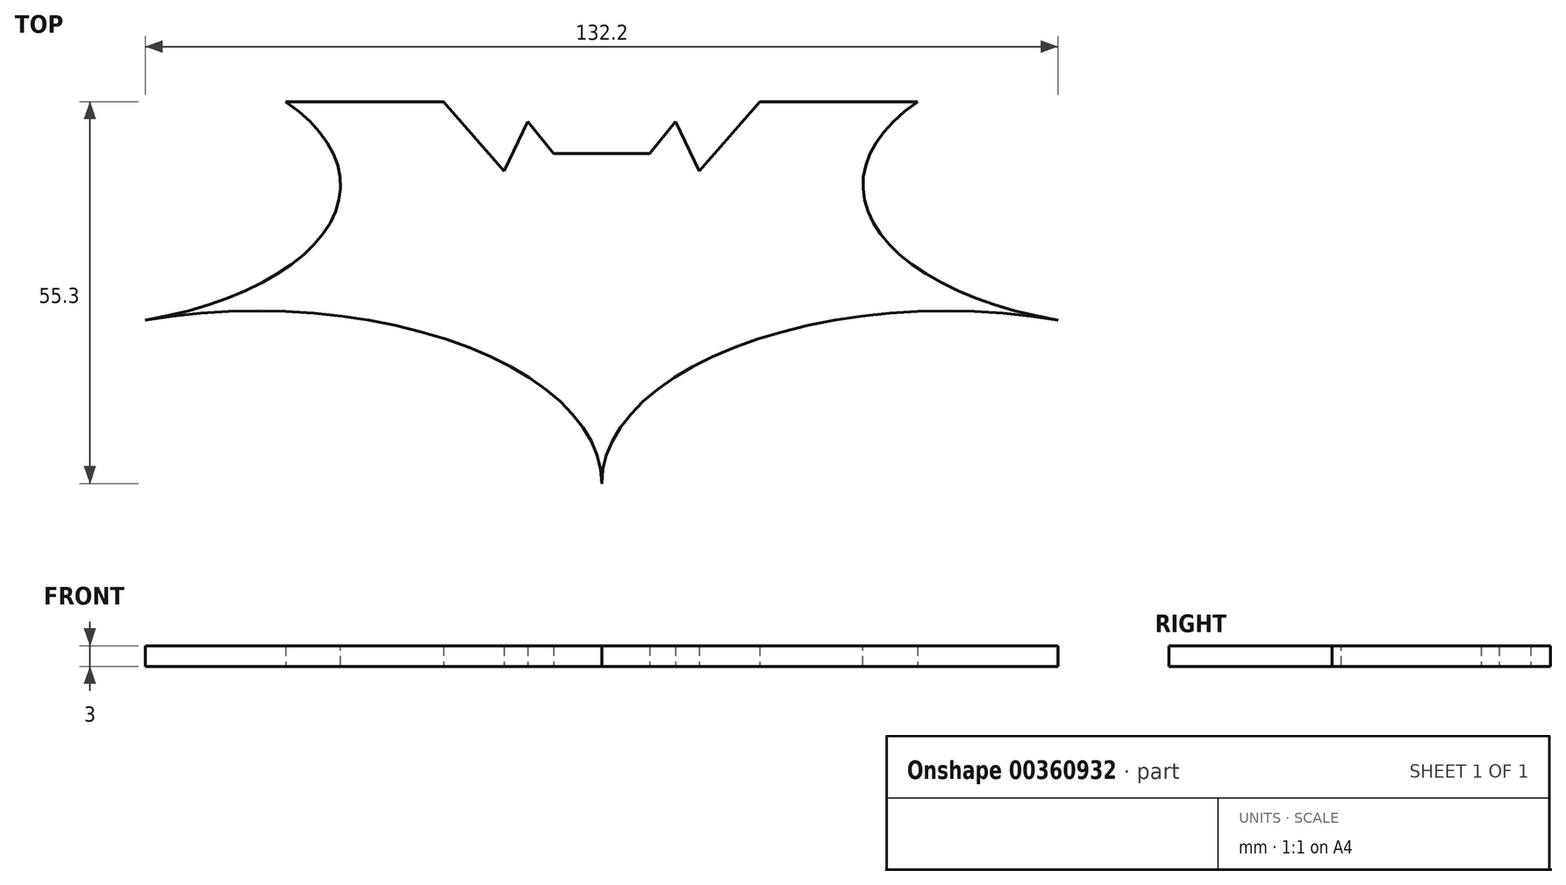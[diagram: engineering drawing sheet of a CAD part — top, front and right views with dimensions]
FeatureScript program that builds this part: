
annotation { "Feature Type Name" : "Feature", "Feature Type Description" : "" }
export const myFeature = defineFeature(function(context is Context, id is Id, definition is map)
    precondition{}
    {
        {
            var Q0;
            Q0=qCreatedBy(makeId("Top.planeOp"),FACE);
            var sketch = newSketch(context, id + "F0", { "sketchPlane" : qUnion([Q0])});
            skLineSegment(sketch, "E0", {"start": v(0, 30) * mm, "end": v(45.74, 30) * mm});
            skEllipticalArc(sketch, "E1", {});
            skEllipticalArc(sketch, "E2", {});
            skLineSegment(sketch, "E3", {"start": v(0, 63.46) * mm, "end": v(0, -66.72) * mm});
            skEllipticalArc(sketch, "E4.MirrorCS", {});
            skEllipticalArc(sketch, "E5.MirrorCS", {});
            skLineSegment(sketch, "E6.MirrorCS", {"start": v(0, 30) * mm, "end": v(-45.74, 30) * mm});
            skLineSegment(sketch, "E7", {"start": v(-22.87, 30) * mm, "end": v(-14.14, 19.94) * mm});
            skLineSegment(sketch, "E8", {"start": v(-14.14, 19.94) * mm, "end": v(-10.69, 27.11) * mm});
            skLineSegment(sketch, "E9", {"start": v(-10.69, 27.11) * mm, "end": v(-6.97, 22.52) * mm});
            skLineSegment(sketch, "E10", {"start": v(-6.97, 22.52) * mm, "end": v(6.97, 22.52) * mm});
            skLineSegment(sketch, "E11", {"start": v(6.97, 22.52) * mm, "end": v(10.7, 27.11) * mm});
            skLineSegment(sketch, "E12", {"start": v(10.7, 27.11) * mm, "end": v(14.14, 19.94) * mm});
            skLineSegment(sketch, "E13", {"start": v(14.14, 19.94) * mm, "end": v(22.87, 30) * mm});
            const initialGuessF0  = {"E1": [0.08, 0.01792409580658342, -1, 0, 0.042171282848956666, 0.020708713304292456, 5.660607123722277, 1.234864980207796], "E2": [0.05, -0.025295858625841085, -1, 0, 0.05, 0.025, 4.3845837415940565, 0], "E4.MirrorCS": [-0.05, -0.025295858625841085, 1, 0, 0.05, 0.025, 6.283185307179586, 1.8986015655855297], "E5.MirrorCS": [-0.08, 0.01792409580658342, 1, 0, 0.042171282848956666, 0.020708713304292456, 5.0483203269717905, 0.6225781834573096]};
            skSetInitialGuess(sketch, initialGuessF0);
            skSolve(sketch);
        }
        {
            var Q0;
            {var subQ5=sQuery(id+"F0.wireOp",EDGE,"E1");Q0=makeQuery(id+"F0.imprint","IMPRINT",FACE,{"disambiguationData":[TD([[makeQuery(id+"F0.imprint","IMPRINT",EDGE,{"derivedFrom":subQ5}),-1.0]])]});}
            var Q1;
            {var subQ3=sQuery(id+"F0.wireOp",EDGE,"E4.MirrorCS");Q1=makeQuery(id+"F0.imprint","IMPRINT",FACE,{"disambiguationData":[TD([[makeQuery(id+"F0.imprint","IMPRINT",EDGE,{"derivedFrom":subQ3}),-1.0]])]});}
            extrude(context, id + "F1", {"entities" : qUnion([Q0, Q1]), "depth" : 3 * mm});
        }
    });
